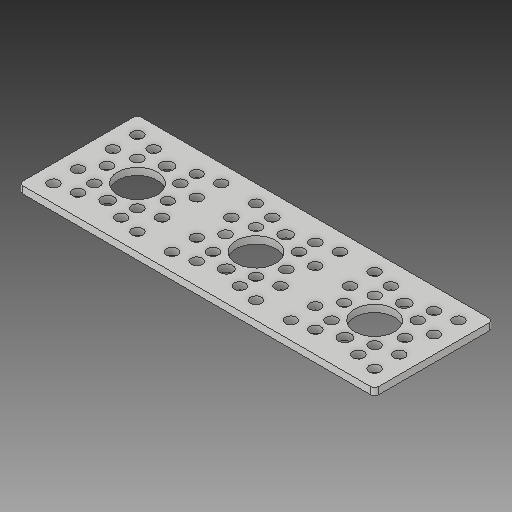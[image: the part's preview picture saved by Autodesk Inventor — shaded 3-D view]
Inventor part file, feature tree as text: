
AUTODESK INVENTOR PART (.ipt)
format: ipt  version: 2017 (Build 210142000, 142)  size: 202,752 bytes
history: native  units: in
note: dims shown in document units (in); Inventor stores cm internally (conversion verified against a paired STEP export)
features: fillet x1
ambient origin geometry x8: Origin, YZ Plane, XZ Plane, XY Plane, X Axis, Y Axis, Z Axis, Center Point
bodies: Solid1 (feature_tree)
feature tree (1):
  fillet  "Fillet1"  [1 undecoded]
note: 1 required parameter value undecoded (feature->parameter linkage not recoverable at this tier; creation-order binding heuristic only, values carry confidence <= 0.55)
